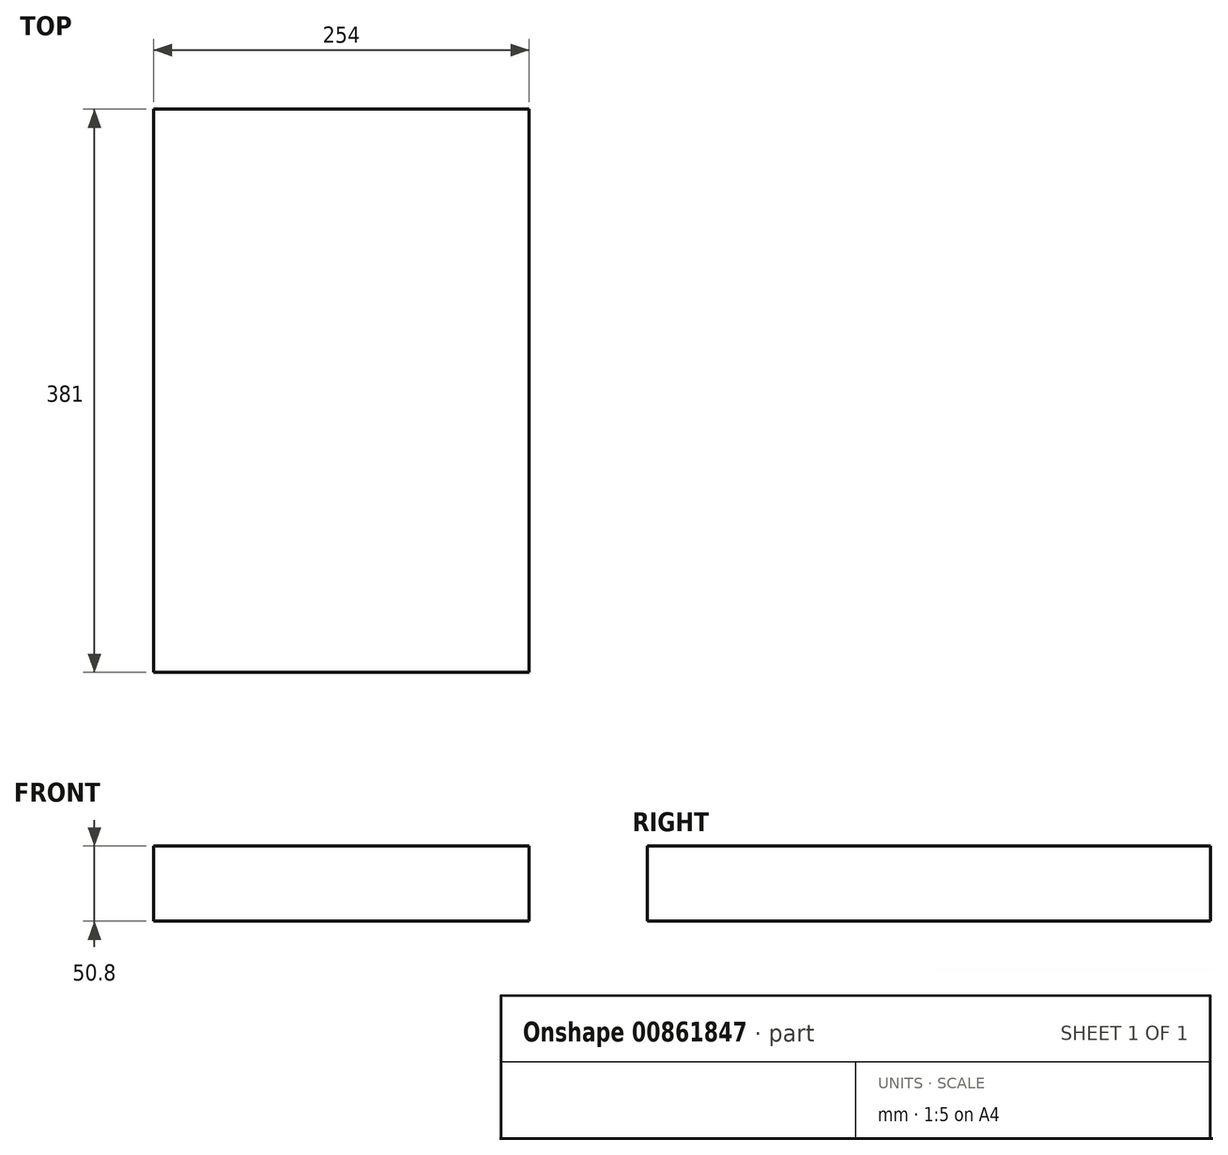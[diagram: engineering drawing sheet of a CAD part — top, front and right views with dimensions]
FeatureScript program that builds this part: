
annotation { "Feature Type Name" : "Feature", "Feature Type Description" : "" }
export const myFeature = defineFeature(function(context is Context, id is Id, definition is map)
    precondition{}
    {
        {
            var Q0;
            Q0=qCreatedBy(makeId("Front.planeOp"),FACE);
            var sketch = newSketch(context, id + "F0", { "sketchPlane" : qUnion([Q0])});
            skLineSegment(sketch, "E0.bottom", {"start": v(127, 25.4) * mm, "end": v(-127, 25.4) * mm});
            skLineSegment(sketch, "E0.top", {"start": v(127, -25.4) * mm, "end": v(-127, -25.4) * mm});
            skLineSegment(sketch, "E0.left", {"start": v(127, 25.4) * mm, "end": v(127, -25.4) * mm});
            skLineSegment(sketch, "E0.right", {"start": v(-127, 25.4) * mm, "end": v(-127, -25.4) * mm});
            skPoint(sketch, "E0.middle", {"position": v(0, 0) * mm});
            skSolve(sketch);
        }
        {
            var Q0;
            Q0 = qSketchRegion(id + "F0", true);
            extrude(context, id + "F1", {"entities" : qUnion([Q0]), "depth" : 381 * mm, "offsetDistance" : 25.4 * mm});
        }
    });
